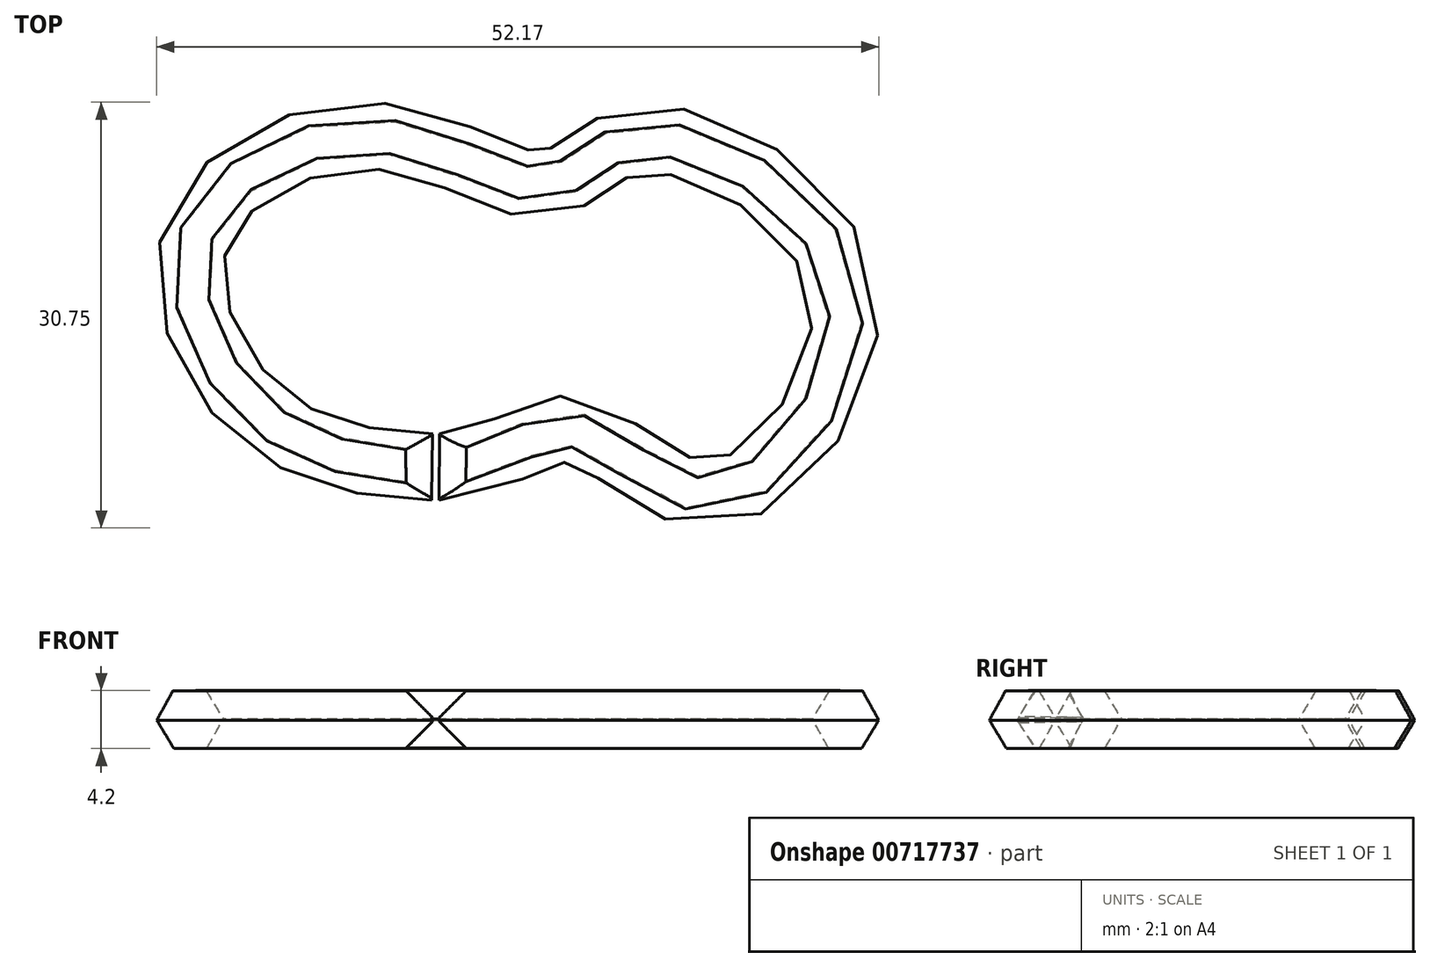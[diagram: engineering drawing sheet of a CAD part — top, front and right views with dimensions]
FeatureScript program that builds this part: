
annotation { "Feature Type Name" : "Feature", "Feature Type Description" : "" }
export const myFeature = defineFeature(function(context is Context, id is Id, definition is map)
    precondition{}
    {
        {
            var Q0;
            Q0=qCreatedBy(makeId("Top.planeOp"),FACE);
            var sketch = newSketch(context, id + "F0", { "sketchPlane" : qUnion([Q0])});
            skFitSpline(sketch, "E0", {"points": [v(0.24, -10.98) * mm, v(9.93, -8.3) * mm, v(20.06, -12.97) * mm, v(29.4, 1.9) * mm, v(14.69, 12.66) * mm, v(7.99, 9.4) * mm, v(-3.78, 12.9) * mm, v(-17.26, 5.96) * mm, v(-12.66, -7.2) * mm, v(-0.28, -10.98) * mm], "startDerivative": vector(134.26, -1.11) * mm, "endDerivative": vector(112.7, -2.06) * mm});
            skSolve(sketch);
        }
        {
            var Q0;
            Q0=qCreatedBy(makeId("Front.planeOp"),FACE);
            var sketch = newSketch(context, id + "F1", { "sketchPlane" : qUnion([Q0])});
            skCircle(sketch, "E1.cCircle", {"center": v(29.6, 0) * mm, "radius": 2.08 * mm, "construction": true});
            skLineSegment(sketch, "E1.0", {"start": v(32, -0.05) * mm, "end": v(30.75, -2.1) * mm});
            skLineSegment(sketch, "E1.1", {"start": v(30.75, -2.1) * mm, "end": v(28.35, -2.06) * mm});
            skLineSegment(sketch, "E1.2", {"start": v(28.35, -2.06) * mm, "end": v(27.2, 0.05) * mm});
            skLineSegment(sketch, "E1.3", {"start": v(27.2, 0.05) * mm, "end": v(28.43, 2.1) * mm});
            skLineSegment(sketch, "E1.4", {"start": v(28.43, 2.1) * mm, "end": v(30.83, 2.06) * mm});
            skLineSegment(sketch, "E1.5", {"start": v(30.83, 2.06) * mm, "end": v(32, -0.05) * mm});
            skPoint(sketch, "E1.0.midPoint", {"position": v(31.37, -1.07) * mm});
            skSolve(sketch);
        }
        {
            var Q0;
            Q0=qCreatedBy(makeId("Front.planeOp"),FACE);
            var sketch = newSketch(context, id + "F2", { "sketchPlane" : qUnion([Q0])});
            skLineSegment(sketch, "E2", {"start": v(0.1, 0) * mm, "end": v(2.5, 2.4) * mm});
            skLineSegment(sketch, "E3", {"start": v(2.41, -2.31) * mm, "end": v(0.1, 0) * mm});
            skLineSegment(sketch, "E4", {"start": v(2.5, 2.4) * mm, "end": v(0, 2.4) * mm});
            skLineSegment(sketch, "E5", {"start": v(2.41, -2.31) * mm, "end": v(0, -2.31) * mm});
            skLineSegment(sketch, "E6", {"start": v(0, -2.31) * mm, "end": v(0, 2.4) * mm});
            skLineSegment(sketch, "E7.MirrorCS", {"start": v(-2.5, 2.4) * mm, "end": v(0, 2.4) * mm});
            skLineSegment(sketch, "E8.MirrorCS", {"start": v(-0.1, 0) * mm, "end": v(-2.5, 2.4) * mm});
            skLineSegment(sketch, "E9.MirrorCS", {"start": v(-2.41, -2.31) * mm, "end": v(-0.1, 0) * mm});
            skLineSegment(sketch, "E10.MirrorCS", {"start": v(-2.41, -2.31) * mm, "end": v(0, -2.31) * mm});
            skSolve(sketch);
        }
        {
            var Q0;
            Q0=makeQuery(id+"F1.imprint","IMPRINT",FACE,{"disambiguationData":[TD([[makeQuery(id+"F1.imprint","IMPRINT",EDGE,{"derivedFrom":sQuery(id+"F1.wireOp",EDGE,"E1.0")}),-1.0]])]});
            var Q1;
            Q1=sQuery(id+"F0.wireOp",EDGE,"E0");
            sweep(context, id + "F3", {"profiles" : qUnion([Q0]), "path" : qUnion([Q1])});
        }
        {
            var Q0;
            Q0 = qSketchRegion(id + "F2", true);
            extrude(context, id + "F4", {"entities" : qUnion([Q0]), "operationType" : NewBodyOperationType.REMOVE, "depth" : 25 * mm, "offsetDistance" : 25 * mm});
        }
    });
